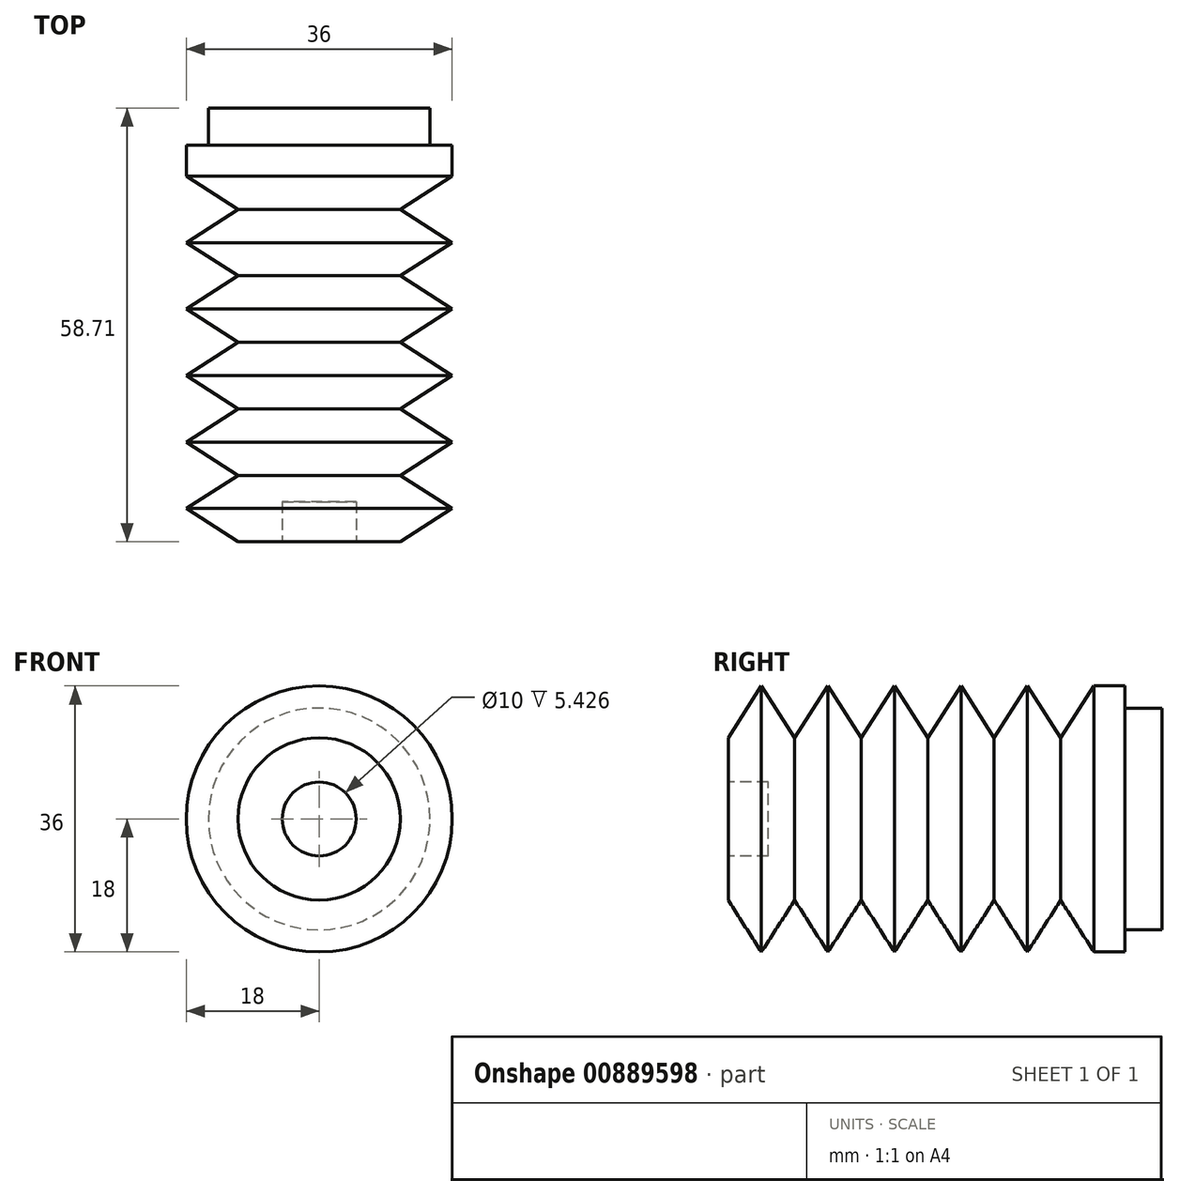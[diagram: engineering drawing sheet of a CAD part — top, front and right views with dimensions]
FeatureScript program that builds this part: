
annotation { "Feature Type Name" : "Feature", "Feature Type Description" : "" }
export const myFeature = defineFeature(function(context is Context, id is Id, definition is map)
    precondition{}
    {
        {
            var Q0;
            Q0=qCreatedBy(makeId("Right.planeOp"),FACE);
            var sketch = newSketch(context, id + "F0", { "sketchPlane" : qUnion([Q0])});
            skLineSegment(sketch, "E0", {"start": v(20.49, 0) * mm, "end": v(20.49, 15) * mm});
            skLineSegment(sketch, "E1", {"start": v(20.49, 15) * mm, "end": v(15.49, 15) * mm});
            skLineSegment(sketch, "E2", {"start": v(15.49, 15) * mm, "end": v(15.49, 18) * mm});
            skLineSegment(sketch, "E3", {"start": v(15.49, 18) * mm, "end": v(11.28, 18) * mm});
            skLineSegment(sketch, "E4", {"start": v(6.78, 19.7) * mm, "end": v(6.78, 9.58) * mm, "construction": true});
            skLineSegment(sketch, "E5", {"start": v(11.28, 18) * mm, "end": v(6.78, 10.99) * mm});
            skLineSegment(sketch, "E6.MirrorCS", {"start": v(2.28, 18) * mm, "end": v(6.78, 10.99) * mm});
            skLineSegment(sketch, "E7.1.0.0", {"start": v(-6.72, 18) * mm, "end": v(-2.22, 10.99) * mm});
            skLineSegment(sketch, "E7.1.0.1", {"start": v(2.28, 18) * mm, "end": v(-2.22, 10.99) * mm});
            skLineSegment(sketch, "E7.2.0.0", {"start": v(-15.72, 18) * mm, "end": v(-11.22, 10.99) * mm});
            skLineSegment(sketch, "E7.2.0.1", {"start": v(-6.72, 18) * mm, "end": v(-11.22, 10.99) * mm});
            skLineSegment(sketch, "E7.3.0.1", {"start": v(-15.72, 18) * mm, "end": v(-20.22, 10.99) * mm});
            skLineSegment(sketch, "E7.direction1", {"start": v(6.78, 10.99) * mm, "end": v(-2.22, 10.99) * mm, "construction": true});
            skLineSegment(sketch, "E8.0.4.0", {"start": v(-33.72, 18) * mm, "end": v(-29.22, 10.99) * mm});
            skLineSegment(sketch, "E8.3.4.0", {"start": v(-24.72, 18) * mm, "end": v(-29.22, 10.99) * mm});
            skLineSegment(sketch, "E8.3.5.0", {"start": v(-33.72, 18) * mm, "end": v(-38.22, 10.99) * mm});
            skLineSegment(sketch, "E9", {"start": v(-24.72, 18) * mm, "end": v(-20.22, 10.99) * mm});
            skLineSegment(sketch, "E10", {"start": v(-38.22, 10.99) * mm, "end": v(-38.22, 5) * mm});
            skLineSegment(sketch, "E11", {"start": v(-38.22, 5) * mm, "end": v(-32.8, 5) * mm});
            skLineSegment(sketch, "E12", {"start": v(-32.8, 5) * mm, "end": v(-32.8, 0) * mm});
            skLineSegment(sketch, "E13", {"start": v(-32.8, 0) * mm, "end": v(20.49, 0) * mm});
            skSolve(sketch);
        }
        {
            var Q0;
            Q0=makeQuery(id+"F0.imprint","IMPRINT",FACE,{"disambiguationData":[TD([[makeQuery(id+"F0.imprint","IMPRINT",EDGE,{"derivedFrom":sQuery(id+"F0.wireOp",EDGE,"E0")}),1.0]])]});
            var Q1;
            Q1=sQuery(id+"F0.wireOp",EDGE,"E13");
            revolve(context, id + "F1", {"surfaceOperationType" : NewSurfaceOperationType.NEW, "entities" : qUnion([Q0]), "axis" : qUnion([Q1]), "revolveType" : RevolveType.FULL});
        }
    });
